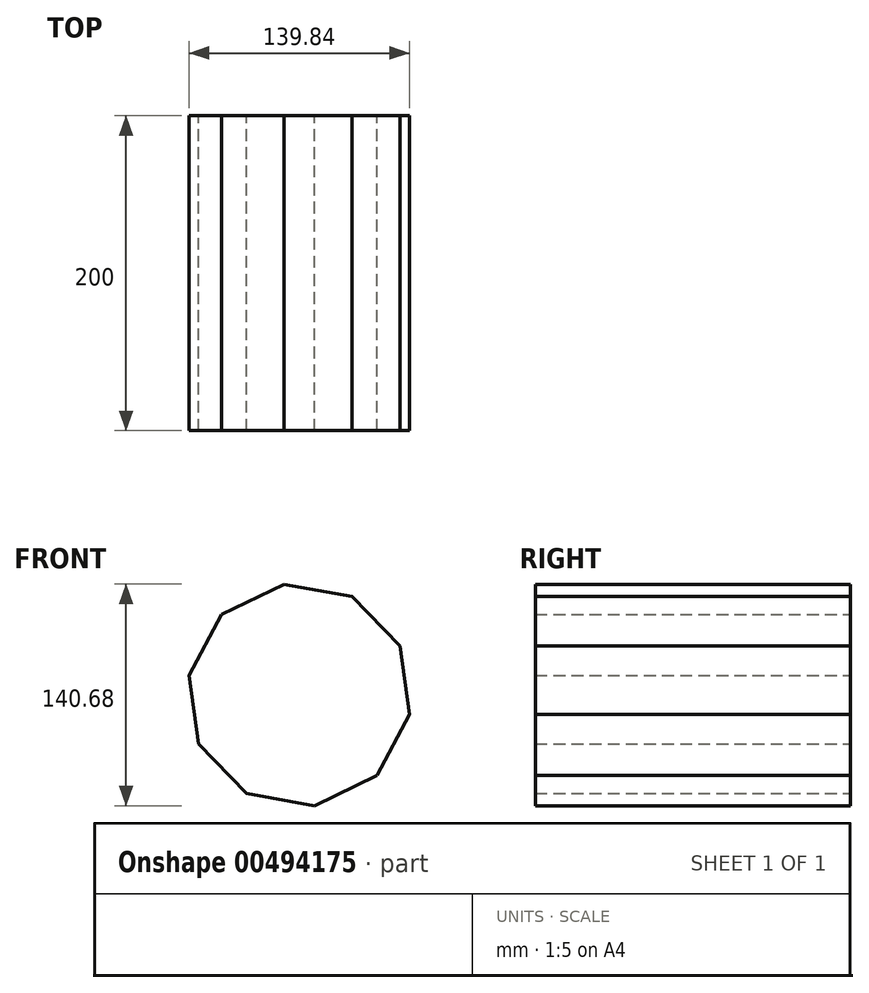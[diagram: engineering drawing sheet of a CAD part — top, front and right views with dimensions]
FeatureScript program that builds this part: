
annotation { "Feature Type Name" : "Feature", "Feature Type Description" : "" }
export const myFeature = defineFeature(function(context is Context, id is Id, definition is map)
    precondition{}
    {
        {
            var Q0;
            Q0=qCreatedBy(makeId("Front.planeOp"),FACE);
            var sketch = newSketch(context, id + "F0", { "sketchPlane" : qUnion([Q0])});
            skCircle(sketch, "E0.cCircle", {"center": v(0, 0) * mm, "radius": 71.02 * mm, "construction": true});
            skLineSegment(sketch, "E0.0", {"start": v(-49.26, 51.15) * mm, "end": v(-9.78, 70.34) * mm});
            skLineSegment(sketch, "E0.1", {"start": v(-9.78, 70.34) * mm, "end": v(33.43, 62.66) * mm});
            skLineSegment(sketch, "E0.2", {"start": v(33.43, 62.66) * mm, "end": v(63.87, 31.04) * mm});
            skLineSegment(sketch, "E0.3", {"start": v(63.87, 31.04) * mm, "end": v(69.92, -12.43) * mm});
            skLineSegment(sketch, "E0.4", {"start": v(69.92, -12.43) * mm, "end": v(49.26, -51.15) * mm});
            skLineSegment(sketch, "E0.5", {"start": v(49.26, -51.15) * mm, "end": v(9.78, -70.34) * mm});
            skLineSegment(sketch, "E0.6", {"start": v(9.78, -70.34) * mm, "end": v(-33.43, -62.66) * mm});
            skLineSegment(sketch, "E0.7", {"start": v(-33.43, -62.66) * mm, "end": v(-63.87, -31.04) * mm});
            skLineSegment(sketch, "E0.8", {"start": v(-63.87, -31.04) * mm, "end": v(-69.92, 12.43) * mm});
            skLineSegment(sketch, "E0.9", {"start": v(-69.92, 12.43) * mm, "end": v(-49.26, 51.15) * mm});
            skSolve(sketch);
        }
        {
            var Q0;
            Q0=makeQuery(id+"F0.imprint","IMPRINT",FACE,{"disambiguationData":[TD([[makeQuery(id+"F0.imprint","IMPRINT",EDGE,{"derivedFrom":sQuery(id+"F0.wireOp",EDGE,"E0.0")}),-1.0]])]});
            extrude(context, id + "F1", {"entities" : qUnion([Q0]), "endBound" : BoundingType.SYMMETRIC, "depth" : 200 * mm});
        }
    });
